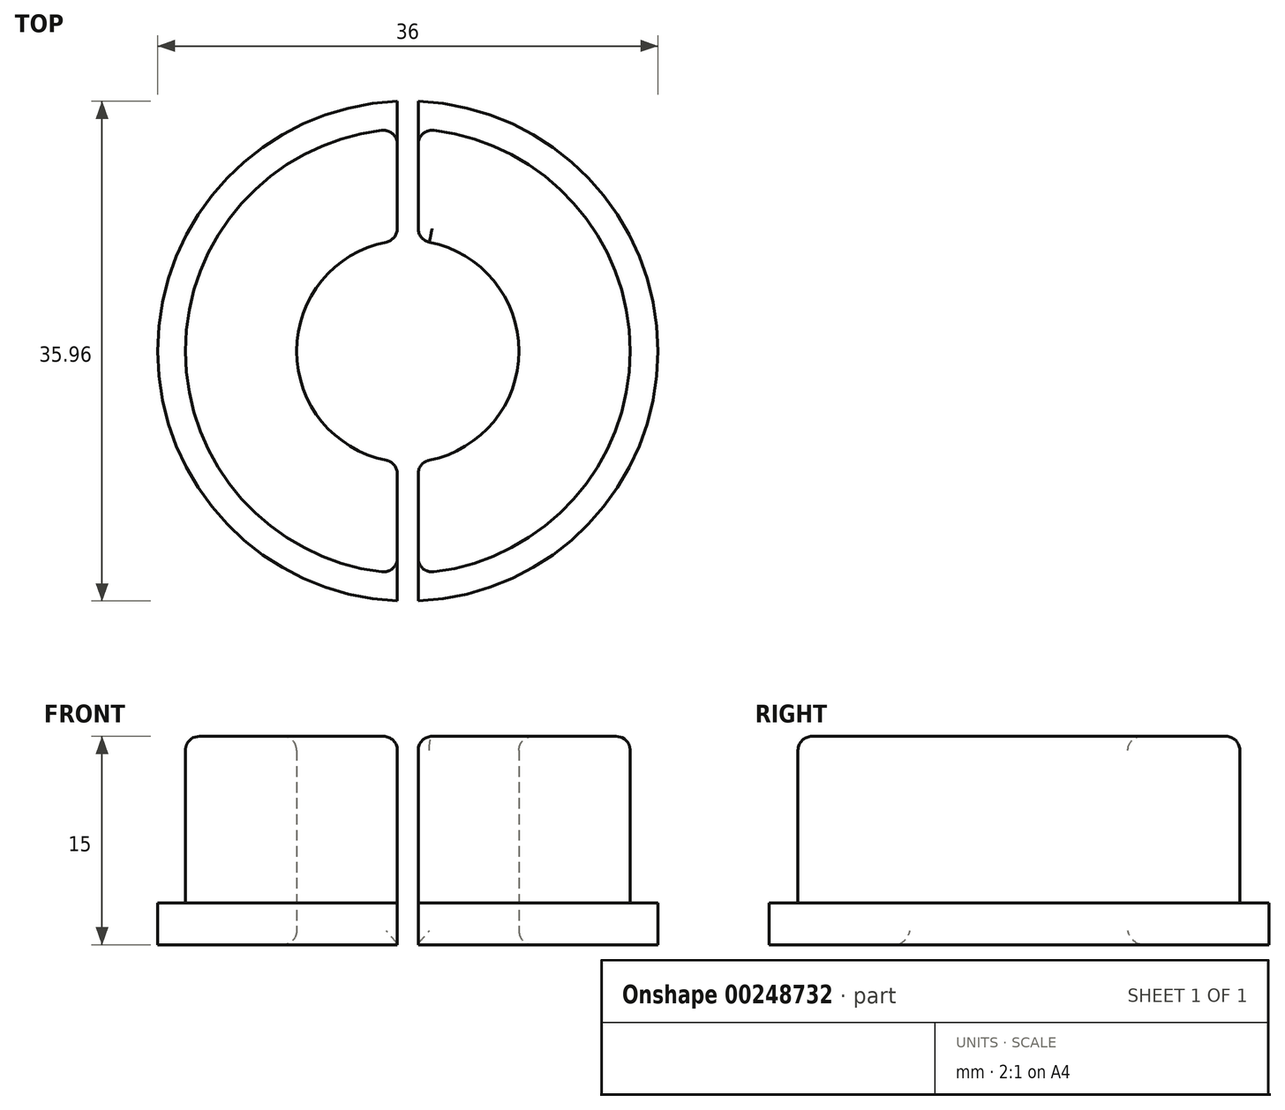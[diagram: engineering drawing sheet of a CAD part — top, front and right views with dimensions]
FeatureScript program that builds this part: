
annotation { "Feature Type Name" : "Feature", "Feature Type Description" : "" }
export const myFeature = defineFeature(function(context is Context, id is Id, definition is map)
    precondition{}
    {
        {
            var Q0;
            Q0=qCreatedBy(makeId("Top.planeOp"),FACE);
            var sketch = newSketch(context, id + "F0", { "sketchPlane" : qUnion([Q0])});
            skCircle(sketch, "E0", {"center": v(0, 0) * mm, "radius": 18 * mm});
            skCircle(sketch, "E1", {"center": v(0, 0) * mm, "radius": 16 * mm});
            skCircle(sketch, "E2", {"center": v(0, 0) * mm, "radius": 8 * mm});
            skSolve(sketch);
        }
        {
            var Q0;
            Q0=makeQuery(id+"F0.imprint","IMPRINT",FACE,{"disambiguationData":[TD([[makeQuery(id+"F0.imprint","IMPRINT",EDGE,{"derivedFrom":sQuery(id+"F0.wireOp",EDGE,"E1")}),1.0]])]});
            extrude(context, id + "F1", {"entities" : qUnion([Q0]), "depth" : 15 * mm});
        }
        {
            var Q0;
            Q0 = qSketchRegion(id + "F0", true);
            extrude(context, id + "F2", {"entities" : qUnion([Q0]), "operationType" : NewBodyOperationType.ADD, "depth" : 3 * mm});
        }
        {
            var Q0;
            Q0=qCreatedBy(makeId("Top.planeOp"),FACE);
            var sketch = newSketch(context, id + "F3", { "sketchPlane" : qUnion([Q0])});
            skLineSegment(sketch, "E3.bottom", {"start": v(0.75, -20) * mm, "end": v(-0.75, -20) * mm});
            skLineSegment(sketch, "E3.top", {"start": v(0.75, 20) * mm, "end": v(-0.75, 20) * mm});
            skLineSegment(sketch, "E3.left", {"start": v(0.75, -20) * mm, "end": v(0.75, 20) * mm});
            skLineSegment(sketch, "E3.right", {"start": v(-0.75, -20) * mm, "end": v(-0.75, 20) * mm});
            skSolve(sketch);
        }
        {
            var Q0;
            Q0 = qSketchRegion(id + "F3", true);
            extrude(context, id + "F4", {"entities" : qUnion([Q0]), "operationType" : NewBodyOperationType.REMOVE, "endBound" : BoundingType.THROUGH_ALL, "depth" : 25 * mm});
        }
        {
            var Q0;
            {var subQ0=sQuery(id+"F0.wireOp",EDGE,"E2");Q0=makeQuery(id+"F4.boolean.opBoolean","SPLIT",EDGE,{"disambiguationData":[TD([makeQuery(id+"F4.opExtrude","SWEPT_FACE",FACE,{"disambiguationData":[OSD([sQuery(id+"F3.wireOp",EDGE,"E3.right")])]})])],"derivedFrom":makeQuery(id+"F1.opExtrude","CAP_EDGE",EDGE,{"disambiguationData":[OSD([subQ0])],"isStart":true})});}
            var Q1;
            {var subQ0=sQuery(id+"F0.wireOp",EDGE,"E2");Q1=makeQuery(id+"F4.boolean.opBoolean","SPLIT",EDGE,{"disambiguationData":[TD([makeQuery(id+"F4.opExtrude","SWEPT_FACE",FACE,{"disambiguationData":[OSD([sQuery(id+"F3.wireOp",EDGE,"E3.left")])]})])],"derivedFrom":makeQuery(id+"F1.opExtrude","CAP_EDGE",EDGE,{"disambiguationData":[OSD([subQ0])],"isStart":true})});}
            var Q2;
            {var subQ0=sQuery(id+"F0.wireOp",EDGE,"E1");var subQ1=sQuery(id+"F0.wireOp",EDGE,"E2");Q2=makeQuery(id+"F4.boolean.opBoolean","SPLIT",FACE,{"disambiguationData":[TD([makeQuery(id+"F4.opExtrude","SWEPT_FACE",FACE,{"disambiguationData":[OSD([sQuery(id+"F3.wireOp",EDGE,"E3.right")])]})])],"derivedFrom":makeQuery(id+"F1.opExtrude","CAP_FACE",FACE,{"disambiguationData":[OSD([subQ0,subQ1])],"isStart":false})});}
            var Q3;
            {var subQ0=sQuery(id+"F0.wireOp",EDGE,"E2");Q3=makeQuery(id+"F4.boolean.opBoolean","SPLIT",EDGE,{"disambiguationData":[TD([makeQuery(id+"F4.opExtrude","SWEPT_FACE",FACE,{"disambiguationData":[OSD([sQuery(id+"F3.wireOp",EDGE,"E3.left")])]})])],"derivedFrom":makeQuery(id+"F1.opExtrude","CAP_EDGE",EDGE,{"disambiguationData":[OSD([subQ0])],"isStart":false})});}
            var Q4;
            {var subQ0=sQuery(id+"F0.wireOp",EDGE,"E1");Q4=makeQuery(id+"F4.boolean.opBoolean","SPLIT",EDGE,{"disambiguationData":[TD([makeQuery(id+"F4.opExtrude","SWEPT_FACE",FACE,{"disambiguationData":[OSD([sQuery(id+"F3.wireOp",EDGE,"E3.left")])]})])],"derivedFrom":makeQuery(id+"F1.opExtrude","CAP_EDGE",EDGE,{"disambiguationData":[OSD([subQ0])],"isStart":false})});}
            var Q5;
            Q5=makeQuery(id+"F4.boolean.opBoolean","INTERSECT",EDGE,{"disambiguationData":[OD(0.0)],"derivedFrom":[makeQuery(id+"F1.opExtrude","CAP_FACE",FACE,{"disambiguationData":[OSD([sQuery(id+"F0.wireOp",EDGE,"E1"),sQuery(id+"F0.wireOp",EDGE,"E2")])],"isStart":false}),makeQuery(id+"F4.opExtrude","SWEPT_FACE",FACE,{"disambiguationData":[OSD([sQuery(id+"F3.wireOp",EDGE,"E3.left")])]})]});
            var Q6;
            Q6=makeQuery(id+"F4.boolean.opBoolean","INTERSECT",EDGE,{"disambiguationData":[OD(1.0)],"derivedFrom":[makeQuery(id+"F1.opExtrude","CAP_FACE",FACE,{"disambiguationData":[OSD([sQuery(id+"F0.wireOp",EDGE,"E1"),sQuery(id+"F0.wireOp",EDGE,"E2")])],"isStart":false}),makeQuery(id+"F4.opExtrude","SWEPT_FACE",FACE,{"disambiguationData":[OSD([sQuery(id+"F3.wireOp",EDGE,"E3.left")])]})]});
            var Q7;
            Q7=makeQuery(id+"F4.boolean.opBoolean","INTERSECT",EDGE,{"disambiguationData":[OD(0.0)],"derivedFrom":[makeQuery(id+"F1.opExtrude","SWEPT_FACE",FACE,{"disambiguationData":[OSD([sQuery(id+"F0.wireOp",EDGE,"E1")])]}),makeQuery(id+"F4.opExtrude","SWEPT_FACE",FACE,{"disambiguationData":[OSD([sQuery(id+"F3.wireOp",EDGE,"E3.right")])]})]});
            var Q8;
            Q8=makeQuery(id+"F4.boolean.opBoolean","INTERSECT",EDGE,{"disambiguationData":[OD(0.0)],"derivedFrom":[makeQuery(id+"F1.opExtrude","SWEPT_FACE",FACE,{"disambiguationData":[OSD([sQuery(id+"F0.wireOp",EDGE,"E1")])]}),makeQuery(id+"F4.opExtrude","SWEPT_FACE",FACE,{"disambiguationData":[OSD([sQuery(id+"F3.wireOp",EDGE,"E3.left")])]})]});
            var Q9;
            Q9=makeQuery(id+"F4.boolean.opBoolean","INTERSECT",EDGE,{"disambiguationData":[OD(1.0)],"derivedFrom":[makeQuery(id+"F1.opExtrude","SWEPT_FACE",FACE,{"disambiguationData":[OSD([sQuery(id+"F0.wireOp",EDGE,"E1")])]}),makeQuery(id+"F4.opExtrude","SWEPT_FACE",FACE,{"disambiguationData":[OSD([sQuery(id+"F3.wireOp",EDGE,"E3.left")])]})]});
            var Q10;
            Q10=makeQuery(id+"F4.boolean.opBoolean","INTERSECT",EDGE,{"disambiguationData":[OD(1.0)],"derivedFrom":[makeQuery(id+"F1.opExtrude","SWEPT_FACE",FACE,{"disambiguationData":[OSD([sQuery(id+"F0.wireOp",EDGE,"E1")])]}),makeQuery(id+"F4.opExtrude","SWEPT_FACE",FACE,{"disambiguationData":[OSD([sQuery(id+"F3.wireOp",EDGE,"E3.right")])]})]});
            var Q11;
            Q11=makeQuery(id+"F4.boolean.opBoolean","INTERSECT",EDGE,{"disambiguationData":[OD(0.0)],"derivedFrom":[makeQuery(id+"F1.opExtrude","SWEPT_FACE",FACE,{"disambiguationData":[OSD([sQuery(id+"F0.wireOp",EDGE,"E2")])]}),makeQuery(id+"F4.opExtrude","SWEPT_FACE",FACE,{"disambiguationData":[OSD([sQuery(id+"F3.wireOp",EDGE,"E3.right")])]})]});
            var Q12;
            Q12=makeQuery(id+"F4.boolean.opBoolean","INTERSECT",EDGE,{"disambiguationData":[OD(0.0)],"derivedFrom":[makeQuery(id+"F1.opExtrude","SWEPT_FACE",FACE,{"disambiguationData":[OSD([sQuery(id+"F0.wireOp",EDGE,"E2")])]}),makeQuery(id+"F4.opExtrude","SWEPT_FACE",FACE,{"disambiguationData":[OSD([sQuery(id+"F3.wireOp",EDGE,"E3.left")])]})]});
            var Q13;
            Q13=makeQuery(id+"F4.boolean.opBoolean","INTERSECT",EDGE,{"disambiguationData":[OD(1.0)],"derivedFrom":[makeQuery(id+"F1.opExtrude","SWEPT_FACE",FACE,{"disambiguationData":[OSD([sQuery(id+"F0.wireOp",EDGE,"E2")])]}),makeQuery(id+"F4.opExtrude","SWEPT_FACE",FACE,{"disambiguationData":[OSD([sQuery(id+"F3.wireOp",EDGE,"E3.left")])]})]});
            var Q14;
            Q14=makeQuery(id+"F4.boolean.opBoolean","INTERSECT",EDGE,{"disambiguationData":[OD(1.0)],"derivedFrom":[makeQuery(id+"F1.opExtrude","SWEPT_FACE",FACE,{"disambiguationData":[OSD([sQuery(id+"F0.wireOp",EDGE,"E2")])]}),makeQuery(id+"F4.opExtrude","SWEPT_FACE",FACE,{"disambiguationData":[OSD([sQuery(id+"F3.wireOp",EDGE,"E3.right")])]})]});
            fillet(context, id + "F5", {"entities" : qUnion([Q0, Q1, Q2, Q3, Q4, Q5, Q6, Q7, Q8, Q9, Q10, Q11, Q12, Q13, Q14]), "radius" : 1 * mm, "tangentPropagation" : true, "allowEdgeOverflow" : false});
        }
    });
